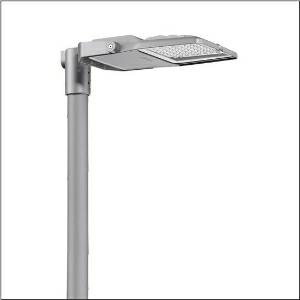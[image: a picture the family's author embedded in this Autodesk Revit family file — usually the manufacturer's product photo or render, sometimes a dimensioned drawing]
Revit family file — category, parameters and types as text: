
# Revit family: floodlight_fl_21_iq_mini___pl33t_5xa7771d4f3a_dbd7
name_source: partatom
category: Lighting Fixtures
units: mm (PartAtom-declared; Revit-internal decimal feet)

## family parameters
Cut with Voids When Loaded = No
Host = Face
Light Source = No
Part Type = Normal
Room Calculation Point = No
Round Connector Dimension = Use Diameter
Shared = No

## types (1)
- --- (1 x LED, 18390 lm, 143 W, 4000K)
    Apparent Load = 143 VA
    CIE Flux Codes = 26 75 99 100 100
    Color Rendering = 70
    Color Temperature = 4000K
    Default Elevation = 1800 mm
    Description = Floodlight FL 21 iQ mini, floodlight, primary light control with lens, of PMMA, primary optical cover: protective disc, of toughened safety glass, transparent, light distribution: PL33T, light emission: direct distribution, installation type: surface-mounted, LED, High Power LED, rated luminous flux: 18.390lm, luminous efficacy: 129lm/W, light colour: 740, colour temperature: 4000K, control gear: iQ Comfort/DALI, control: Auto-Match, Temp-Guard, Lumen-Switch, Night-Set, Smart-Wire, Light-Fading, Desk-Remote (wireless, voltage-free reading and setting of iQ features in the workshop via application-optimized NFC function/RFID function), optimised constant luminous flux control (CLO 2.0), with terminal, 6-pole, mains connection: 220..240V, AC, 50/60Hz, start of lifetime: 143W, end of service life: 152W, reduction: 61W, luminaire housing, of diecast aluminium, powder-coated, Siteco® metallic grey (DB 702S), corrosivity category C5 mid according to DIN EN ISO 12944, suitable for swimming pools, chlorine-resistant, sealing non-destructively replaceable, please order mast flange separately, mast bracket, of steel, galvanised, powder-coated, Siteco® metallic grey (DB 702S), protection rating (complete): IP66, insulation class (complete): insulation class II (safety insulation), certification: CE, ENEC, VDE, protection symbol: D, impact resistance: IK08, permissible operating ambient temperature: -40..+40°C, permissible operating ambient temperature for outdoor applications: -40..+50°C, standard: DIN EN 12944, LABS conformity tested according to VDMA 24364:2018-05, packaging unit: 1 piece

Light Distribution: PL33T
    Height = 70 mm
    Lamp = 1 x LED
    Lamp Light Flux = 18390 lm
    Lamp Power = 143 W
    Lamp count = 1
    Length = 485 mm
    Luminous efficacy = 129 lm/W
    Manufacturer = Siteco
    ModVariant = No
    Model = 5XA7771D4F3A
    Number of Poles = 1
    OnlyDefault = Yes
    Power Factor = 1
    Product Name = Floodlight FL 21 iQ mini | PL33T
    Product group = floodlight | pylon annexe
    ProductGroupID = 6201
    Protection Class = Protection class II
    Protection Degree = IP 66
    RLX_Detail_Level = 1
    RLX_Emergency_Light_Flux = 0 lm
    RLX_Emergency_Type = 0
    RLX_Emergency_Type_DB = No
    RlxData = <blob elided: 101653 chars, md5=4e261fd4>
    Socket = socket
    Standby Power = 0 W
    System Light Flux = 18390 lm
    System Power = 143 W
    Type Comments = factory setting: luminous flux: 100 % | dim-lin: 254 | 730 mA
    Type Image = l_1007125.jpg
    URL = http://relux.com
    VarID = @adj_170525
    Voltage = 0 V
    Weight = 0.00 kg
    Width = 337 mm

## geometry (parser evidence)
native form markers: Blend x4, Sweep x13
no freeform markers — native parametric forms only
